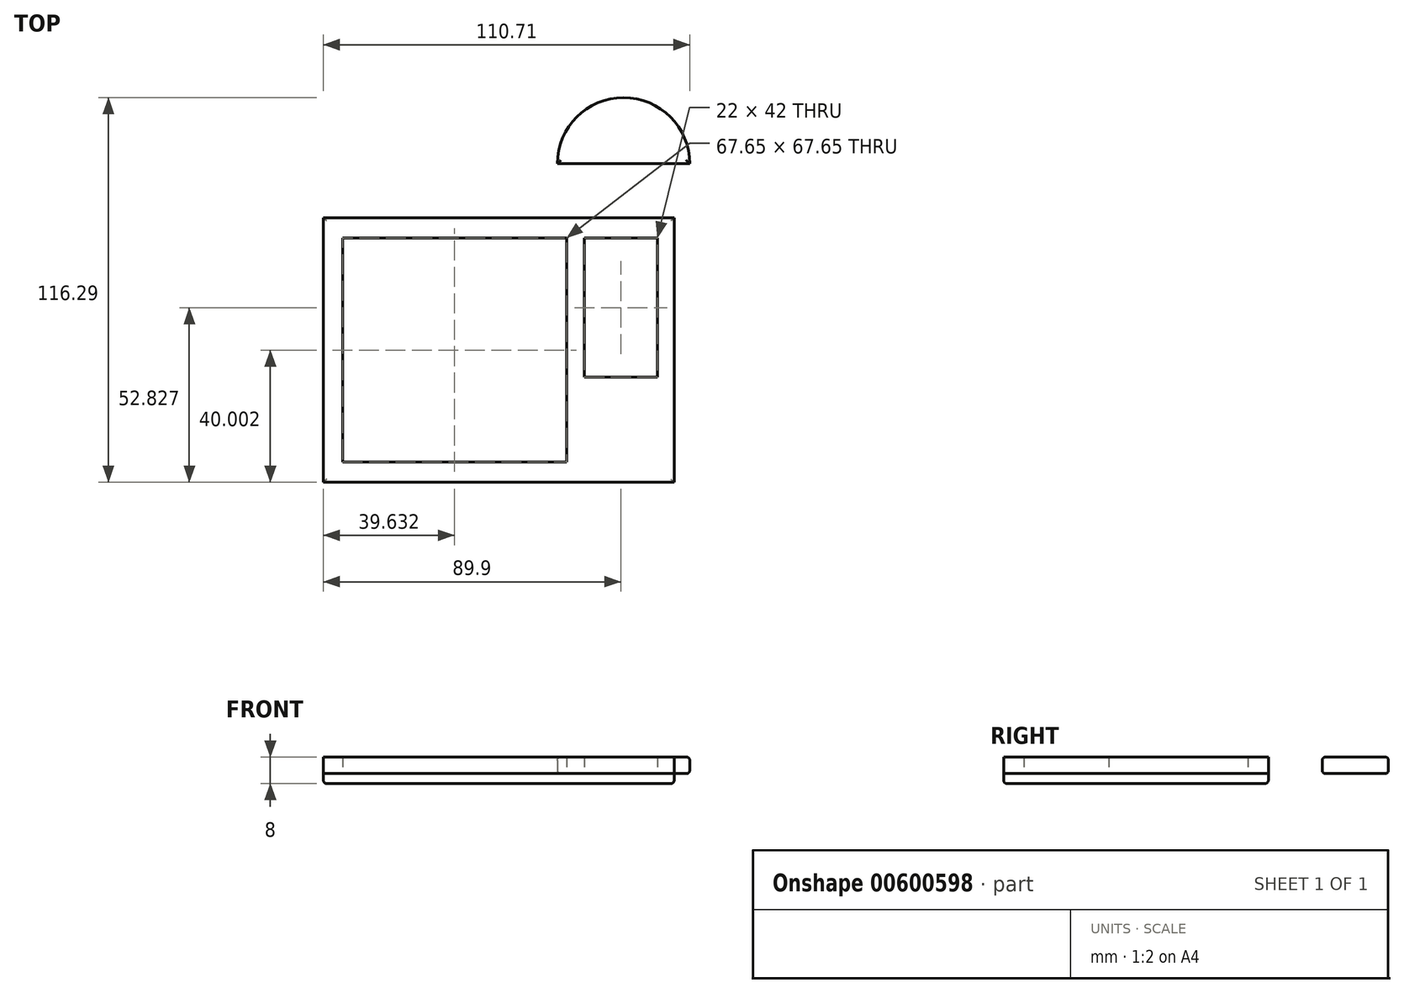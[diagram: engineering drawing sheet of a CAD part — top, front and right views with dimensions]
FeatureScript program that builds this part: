
annotation { "Feature Type Name" : "Feature", "Feature Type Description" : "" }
export const myFeature = defineFeature(function(context is Context, id is Id, definition is map)
    precondition{}
    {
        {
            var Q0;
            Q0=qCreatedBy(makeId("Top.planeOp"),FACE);
            var sketch = newSketch(context, id + "F0", { "sketchPlane" : qUnion([Q0])});
            skCircle(sketch, "E0", {"center": v(0, 0) * mm, "radius": 20 * mm});
            skLineSegment(sketch, "E1", {"start": v(-20, 0) * mm, "end": v(20, 0) * mm});
            skSolve(sketch);
        }
        {
            var Q0;
            {var subQ0=sQuery(id+"F0.wireOp",EDGE,"E1");Q0=makeQuery(id+"F0.imprint","IMPRINT",FACE,{"disambiguationData":[TD([[makeQuery(id+"F0.imprint","IMPRINT",EDGE,{"derivedFrom":subQ0}),1.0]])]});}
            extrude(context, id + "F1", {"entities" : qUnion([Q0]), "depth" : 5 * mm, "offsetDistance" : 25 * mm});
        }
        {
            var Q0;
            Q0=qCreatedBy(makeId("Top.planeOp"),FACE);
            var sketch = newSketch(context, id + "F2", { "sketchPlane" : qUnion([Q0])});
            skLineSegment(sketch, "E2.bottom", {"start": v(15.29, -16.29) * mm, "end": v(-90.71, -16.29) * mm});
            skLineSegment(sketch, "E2.top", {"start": v(15.29, -96.29) * mm, "end": v(-90.71, -96.29) * mm});
            skLineSegment(sketch, "E2.left", {"start": v(15.29, -16.29) * mm, "end": v(15.29, -96.29) * mm});
            skLineSegment(sketch, "E2.right", {"start": v(-90.71, -16.29) * mm, "end": v(-90.71, -96.29) * mm});
            skPoint(sketch, "E2.middle", {"position": v(-37.71, -56.29) * mm});
            skLineSegment(sketch, "E3", {"start": v(-37.71, -56.29) * mm, "end": v(-90.71, -56.29) * mm});
            skLineSegment(sketch, "E4.bottom", {"start": v(-84.9, -22.46) * mm, "end": v(-17.25, -22.46) * mm});
            skLineSegment(sketch, "E4.top", {"start": v(-84.9, -90.11) * mm, "end": v(-17.25, -90.11) * mm});
            skLineSegment(sketch, "E4.left", {"start": v(-84.9, -22.46) * mm, "end": v(-84.9, -90.11) * mm});
            skLineSegment(sketch, "E4.right", {"start": v(-17.25, -22.46) * mm, "end": v(-17.25, -90.11) * mm});
            skPoint(sketch, "E4.middle", {"position": v(-51.08, -56.29) * mm});
            skLineSegment(sketch, "E5.bottom", {"start": v(-11.8, -22.46) * mm, "end": v(10.2, -22.46) * mm});
            skLineSegment(sketch, "E5.top", {"start": v(-11.8, -64.46) * mm, "end": v(10.2, -64.46) * mm});
            skLineSegment(sketch, "E5.left", {"start": v(-11.8, -22.46) * mm, "end": v(-11.8, -64.46) * mm});
            skLineSegment(sketch, "E5.right", {"start": v(10.2, -22.46) * mm, "end": v(10.2, -64.46) * mm});
            skLineSegment(sketch, "E6.bottom", {"start": v(-90.71, -96.29) * mm, "end": v(15.29, -96.29) * mm});
            skLineSegment(sketch, "E6.top", {"start": v(-90.71, -16.29) * mm, "end": v(15.29, -16.29) * mm});
            skLineSegment(sketch, "E6.left", {"start": v(-90.71, -96.29) * mm, "end": v(-90.71, -16.29) * mm});
            skLineSegment(sketch, "E6.right", {"start": v(15.29, -96.29) * mm, "end": v(15.29, -16.29) * mm});
            skLineSegment(sketch, "E7.bottom", {"start": v(15.29, -16.29) * mm, "end": v(121.29, -16.29) * mm});
            skLineSegment(sketch, "E7.top", {"start": v(15.29, -96.29) * mm, "end": v(121.29, -96.29) * mm});
            skLineSegment(sketch, "E7.right", {"start": v(121.29, -16.29) * mm, "end": v(121.29, -96.29) * mm});
            skSolve(sketch);
        }
        {
            var Q0;
            {var subQ1=sQuery(id+"F2.wireOp",EDGE,"E4.bottom");Q0=makeQuery(id+"F2.imprint","IMPRINT",FACE,{"disambiguationData":[TD([[makeQuery(id+"F2.imprint","IMPRINT",EDGE,{"derivedFrom":subQ1}),1.0]])]});}
            extrude(context, id + "F3", {"entities" : qUnion([Q0]), "depth" : 5 * mm, "offsetDistance" : 25 * mm});
        }
        {
            var Q0;
            Q0=makeQuery(id+"F2.imprint","IMPRINT",FACE,{"disambiguationData":[TD([[makeQuery(id+"F2.imprint","IMPRINT",EDGE,{"derivedFrom":sQuery(id+"F2.wireOp",EDGE,"E7.bottom")}),-1.0]])]});
            extrude(context, id + "F4", {"entities" : qUnion([Q0]), "oppositeDirection" : true, "depth" : 3 * mm, "offsetDistance" : 25 * mm});
        }
        {
            var Q0;
            Q0=makeQuery(id+"F4.opExtrude","SWEPT_BODY",BODY,{"disambiguationData":[OSD([sQuery(id+"F2.wireOp",EDGE,"E7.bottom"),sQuery(id+"F2.wireOp",EDGE,"E7.top"),sQuery(id+"F2.wireOp",EDGE,"E2.left"),sQuery(id+"F2.wireOp",EDGE,"E7.right")])]});
            var Q1;
            Q1=sQuery(id+"F2.wireOp",EDGE,"E2.top");
            transform(context, id + "F5", {"entities" : qUnion([Q0]), "transformType" : TransformType.TRANSLATION_ENTITY, "oppositeDirectionEntity" : false, "transformLine" : qUnion([Q1]), "makeCopy" : false});
        }
        {
            var Q0;
            Q0=makeQuery(id+"F1.opExtrude","CAP_EDGE",EDGE,{"disambiguationData":[OSD([sQuery(id+"F0.wireOp",EDGE,"E0")])],"isStart":true});
            var Q1;
            Q1=makeQuery(id+"F1.opExtrude","CAP_EDGE",EDGE,{"disambiguationData":[OSD([sQuery(id+"F0.wireOp",EDGE,"E1")])],"isStart":true});
            var Q2;
            Q2=makeQuery(id+"F1.opExtrude","CAP_EDGE",EDGE,{"disambiguationData":[OSD([sQuery(id+"F0.wireOp",EDGE,"E0")])],"isStart":false});
            var Q3;
            Q3=makeQuery(id+"F1.opExtrude","CAP_EDGE",EDGE,{"disambiguationData":[OSD([sQuery(id+"F0.wireOp",EDGE,"E1")])],"isStart":false});
            fillet(context, id + "F6", {"entities" : qUnion([Q0, Q1, Q2, Q3]), "radius" : 1 * mm, "tangentPropagation" : true, "allowEdgeOverflow" : false});
        }
        {
            var Q0;
            Q0=makeQuery(id+"F4.opExtrude","CAP_FACE",FACE,{"disambiguationData":[OSD([sQuery(id+"F2.wireOp",EDGE,"E7.bottom"),sQuery(id+"F2.wireOp",EDGE,"E7.top"),sQuery(id+"F2.wireOp",EDGE,"E2.left"),sQuery(id+"F2.wireOp",EDGE,"E7.right")])],"isStart":false});
            var Q1;
            Q1=makeQuery(id+"F3.opExtrude","CAP_EDGE",EDGE,{"disambiguationData":[OSD([sQuery(id+"F2.wireOp",EDGE,"E6.bottom")])],"isStart":false});
            var Q2;
            Q2=makeQuery(id+"F3.opExtrude","CAP_EDGE",EDGE,{"disambiguationData":[OSD([sQuery(id+"F2.wireOp",EDGE,"E6.left")])],"isStart":false});
            var Q3;
            Q3=makeQuery(id+"F3.opExtrude","CAP_EDGE",EDGE,{"disambiguationData":[OSD([sQuery(id+"F2.wireOp",EDGE,"E6.top")])],"isStart":false});
            var Q4;
            Q4=makeQuery(id+"F3.opExtrude","CAP_EDGE",EDGE,{"disambiguationData":[OSD([sQuery(id+"F2.wireOp",EDGE,"E2.left")])],"isStart":false});
            fillet(context, id + "F7", {"entities" : qUnion([Q0, Q1, Q2, Q3, Q4]), "radius" : 1 * mm, "tangentPropagation" : true, "allowEdgeOverflow" : false});
        }
    });
